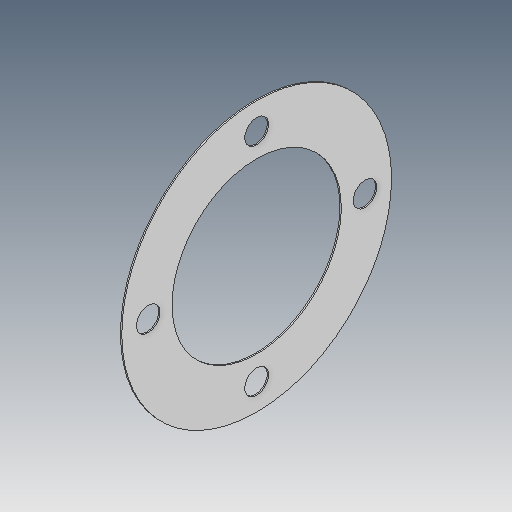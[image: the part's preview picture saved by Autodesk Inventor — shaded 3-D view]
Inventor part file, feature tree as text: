
AUTODESK INVENTOR PART (.ipt)
format: ipt  version: 2025 (Build 290162000, 162)  size: 304,640 bytes
history: native  units: in
note: dims shown in document units (in); Inventor stores cm internally (conversion verified against a paired STEP export)
features: sketch x2, extrude x1
ambient origin geometry x8: Origin, YZ Plane, XZ Plane, XY Plane, X Axis, Y Axis, Z Axis, Center Point
bodies: 实体1 (feature_tree)
feature tree (3):
  extrude  "拉伸1"  Depth=2.5197in
  sketch  "草图1"  dims[d0=0.3543in d2=2.5197in]
  sketch  "草图 - 环形阵列1"  dims[d1=4.0157in d3=2.5197in d4=0.3543in d5=1.6142in d6=1.5748in d8=360.0deg d10=0.0197in d11=0.0in]
